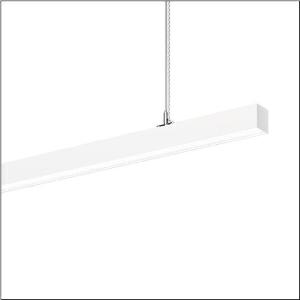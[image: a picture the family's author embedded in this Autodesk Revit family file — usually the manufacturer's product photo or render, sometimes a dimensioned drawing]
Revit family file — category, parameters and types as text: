
# Revit family: silica_r__21_51mx33tbt9w_4d61
name_source: partatom
category: Lighting Fixtures
units: mm (PartAtom-declared; Revit-internal decimal feet)

## family parameters
Cut with Voids When Loaded = No
Host = Face
Light Source = No
Part Type = Normal
Room Calculation Point = No
Round Connector Dimension = Use Diameter
Shared = No

## types (1)
- --- (1 x LED, 7170 lm, 67.4 W, 6500K)
    Apparent Load = 67 VA
    CIE Flux Codes = 78 96 99 56 100
    Color Rendering = 80
    Color Temperature = 6500K
    Default Elevation = 1800 mm
    Description = Silica® 21, office luminaire, primary optical cover: prismatic diffuser, of PMMA, CAT 2 (L<= 3000cd/m²), light emission: direct/indirect distribution, primary light characteristic: symmetric, installation type: suspended mounting, LED, rated luminous flux: 7.170lm, luminous efficacy: 101lm/W, light colour: 8tw, colour temperature: 2700..6500K, control gear: ECG DALI, with terminal, 3+2-pole, max. 2.5mm², mains connection: 220..240V, AC, 50/60Hz, rated input power: 70.8W, luminaire housing, of aluminium, traffic white (RAL 9016), length: 1.504mm, width: 53mm, height: 53mm, protection rating (complete): IP20, insulation class (complete): insulation class I (protective earthing), certification: CE, permissible operating ambient temperature: 0..+35°C, standard: EN 50419, packaging unit: 1 piece
    Height = 53 mm
    Lamp = 1 x LED
    Lamp Light Flux = 7170 lm
    Lamp Power = 67.4 W
    Lamp count = 1
    Length = 1504 mm
    Luminous efficacy = 106 lm/W
    Manufacturer = Siteco
    ModVariant = No
    Model = 51MX33TBT9W
    Mounting Place = Ceiling
    Mounting Type = Pendant
    Number of Poles = 1
    OnlyDefault = Yes
    Power Factor = 1
    Product Name = Silica® 21
    Product group = office luminaire | ceiling pendant
    ProductGroupID = 902
    Protection Class = Protection class I
    Protection Degree = IP 20
    RLX_Detail_Level = 1
    RLX_Emergency_Light_Flux = 0 lm
    RLX_Emergency_Type = 0
    RLX_Emergency_Type_DB = No
    RlxData = <blob elided: 18209 chars, md5=58dd6a97>
    Socket = socket
    Standby Power = 0 W
    System Light Flux = 7170 lm
    System Power = 67 W
    Type Comments = individual setting
    Type Image = l_1313629.jpg
    URL = http://relux.com
    VarID = @adj_089145
    Voltage = 0 V
    Weight = 0.00 kg
    Width = 53 mm

## geometry (parser evidence)
native form markers: Blend x4, Sweep x13
no freeform markers — native parametric forms only
